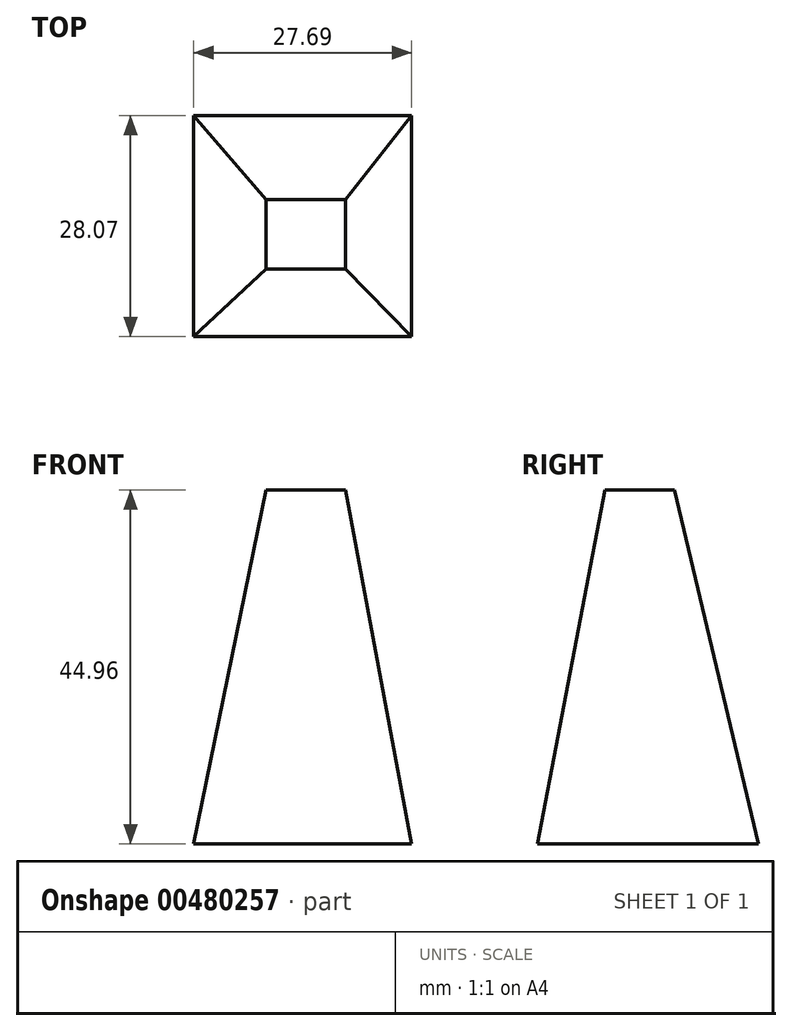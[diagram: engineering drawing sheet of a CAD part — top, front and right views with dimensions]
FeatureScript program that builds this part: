
annotation { "Feature Type Name" : "Feature", "Feature Type Description" : "" }
export const myFeature = defineFeature(function(context is Context, id is Id, definition is map)
    precondition{}
    {
        {
            var Q0;
            Q0=qCreatedBy(makeId("Front.planeOp"),FACE);
            var sketch = newSketch(context, id + "F0", { "sketchPlane" : qUnion([Q0])});
            skArc(sketch, "E0", {"start": v(-3.44, 30.17) * mm, "mid": v(-12.54, 38.49) * mm, "end": v(-23.3, 32.46) * mm});
            skLineSegment(sketch, "E1", {"start": v(-23.3, 32.46) * mm, "end": v(-3.44, 30.17) * mm});
            skSolve(sketch);
        }
        {
            var Q0;
            Q0 = qSketchRegion(id + "F0", true);
            var Q1;
            Q1=sQuery(id+"F0.wireOp",EDGE,"E1");
            revolve(context, id + "F1", {"entities" : qUnion([Q0]), "axis" : qUnion([Q1]), "revolveType" : RevolveType.FULL});
        }
        {
            var Q0;
            Q0=qCreatedBy(makeId("Top.planeOp"),FACE);
            var sketch = newSketch(context, id + "F2", { "sketchPlane" : qUnion([Q0])});
            skLineSegment(sketch, "E2.bottom", {"start": v(10.31, -10.88) * mm, "end": v(38, -10.88) * mm});
            skLineSegment(sketch, "E2.top", {"start": v(10.31, 17.19) * mm, "end": v(38, 17.19) * mm});
            skLineSegment(sketch, "E2.left", {"start": v(10.31, -10.88) * mm, "end": v(10.31, 17.19) * mm});
            skLineSegment(sketch, "E2.right", {"start": v(38, -10.88) * mm, "end": v(38, 17.19) * mm});
            skSolve(sketch);
        }
        {
            var Q0;
            Q0 = qSketchRegion(id + "F2", true);
            extrude(context, id + "F3", {"entities" : qUnion([Q0]), "depth" : 44.96 * mm});
        }
        {
            var Q0;
            Q0=makeQuery(id+"F3.opExtrude","CAP_FACE",FACE,{"disambiguationData":[OSD([sQuery(id+"F2.wireOp",EDGE,"E2.bottom"),sQuery(id+"F2.wireOp",EDGE,"E2.top"),sQuery(id+"F2.wireOp",EDGE,"E2.left"),sQuery(id+"F2.wireOp",EDGE,"E2.right")])],"isStart":false});
            var sketch = newSketch(context, id + "F4", { "sketchPlane" : qUnion([Q0])});
            skLineSegment(sketch, "E3.bottom", {"start": v(19.48, 6.5) * mm, "end": v(29.6, 6.5) * mm});
            skLineSegment(sketch, "E3.top", {"start": v(19.48, -2.3) * mm, "end": v(29.6, -2.3) * mm});
            skLineSegment(sketch, "E3.left", {"start": v(19.48, 6.5) * mm, "end": v(19.48, -2.3) * mm});
            skLineSegment(sketch, "E3.right", {"start": v(29.6, 6.5) * mm, "end": v(29.6, -2.3) * mm});
            skSolve(sketch);
        }
        {
            var Q1;
            Q1=makeQuery(id+"F4.imprint","IMPRINT",FACE,{"disambiguationData":[TD([[makeQuery(id+"F4.imprint","IMPRINT",EDGE,{"derivedFrom":sQuery(id+"F4.wireOp",EDGE,"E3.bottom")}),-1.0]])]});
            var Q2;
            Q2=makeQuery(id+"F3.opExtrude","CAP_FACE",FACE,{"disambiguationData":[OSD([sQuery(id+"F2.wireOp",EDGE,"E2.bottom"),sQuery(id+"F2.wireOp",EDGE,"E2.top"),sQuery(id+"F2.wireOp",EDGE,"E2.left"),sQuery(id+"F2.wireOp",EDGE,"E2.right")])],"isStart":true});
            loft(context, id + "F5", {"operationType" : NewBodyOperationType.INTERSECT, "sheetProfilesArray" : [{ "sheetProfileEntities" : qUnion([Q1]) }, { "sheetProfileEntities" : qUnion([Q2]) }]});
        }
    });
